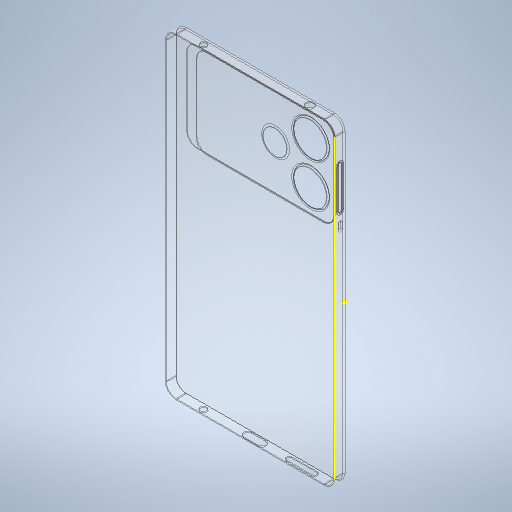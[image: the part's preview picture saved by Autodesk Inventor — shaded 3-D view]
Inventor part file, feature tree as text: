
AUTODESK INVENTOR PART (.ipt)
format: ipt  version: 2025.2 (Build 292293000, 293)  size: 430,080 bytes
history: native  units: in
note: dims shown in document units (in); Inventor stores cm internally (conversion verified against a paired STEP export)
features: sketch x13, extrude x10, fillet x2, shell x1, plane x1
ambient origin geometry x8: Origin, YZ Plane, XZ Plane, XY Plane, X Axis, Y Axis, Z Axis, Center Point
bodies: Solid1 (feature_tree)
feature tree (27):
  extrude  "Extrusion1"  Depth=5.9055in
  shell  "Shell1"  Thickness=0.1969in
  extrude  "Extrusion2"  Depth=0.0197in
  sketch  "Sketch3"  dims[d6=0.011in d7=0.0in d8=0.0394in d9=0.0in]
  sketch  "Sketch4"  dims[d10=0.0197in d11=0.011in d12=0.0in]
  extrude  "Extrusion3"  Depth=0.011in TaperAngle=0.0deg
  fillet  "Face Fillet1"
  extrude  "Extrusion4"  Depth=0.011in TaperAngle=0.0deg
  extrude  "Extrusion5"  Depth=1.6535in
  extrude  "Extrusion6"  Depth=0.011in TaperAngle=0.0deg
  extrude  "Extrusion7"  Depth=0.0157in TaperAngle=0.0deg
  extrude  "Extrusion8"  Depth=0.7087in
  fillet  "Fillet1"  Radius=0.7087in
  extrude  "Extrusion9"  Depth=0.0197in
  extrude  "Extrusion10"  Depth=0.1969in TaperAngle=0.0deg
  plane  "Work Plane1"
  sketch  "Sketch13"
  sketch  "Sketch1"  dims[d0=3.1496in d1=5.9055in d2=0.1969in]
  sketch  "Sketch2"  dims[d3=0.1969in d4=0.0in d5=0.0197in]
  sketch  "Sketch5"  dims[d13=2.7559in d14=1.6535in]
  sketch  "Sketch6"  dims[d15=0.1969in d16=0.011in d17=0.0in]
  sketch  "Sketch7"  dims[d18=0.1969in d19=0.0157in d20=0.0in]
  sketch  "Sketch8"  dims[d21=0.0in d22=0.0in d23=0.7087in d24=0.7087in]
  sketch  "Sketch9"  dims[d25=0.0157in d26=0.0in d27=0.0197in]
  sketch  "Sketch10"  dims[d28=0.0787in d29=0.0in d30=0.1969in d31=0.0in]
  sketch  "Sketch11"  dims[d32=0.1969in]
  sketch  "Sketch12"
